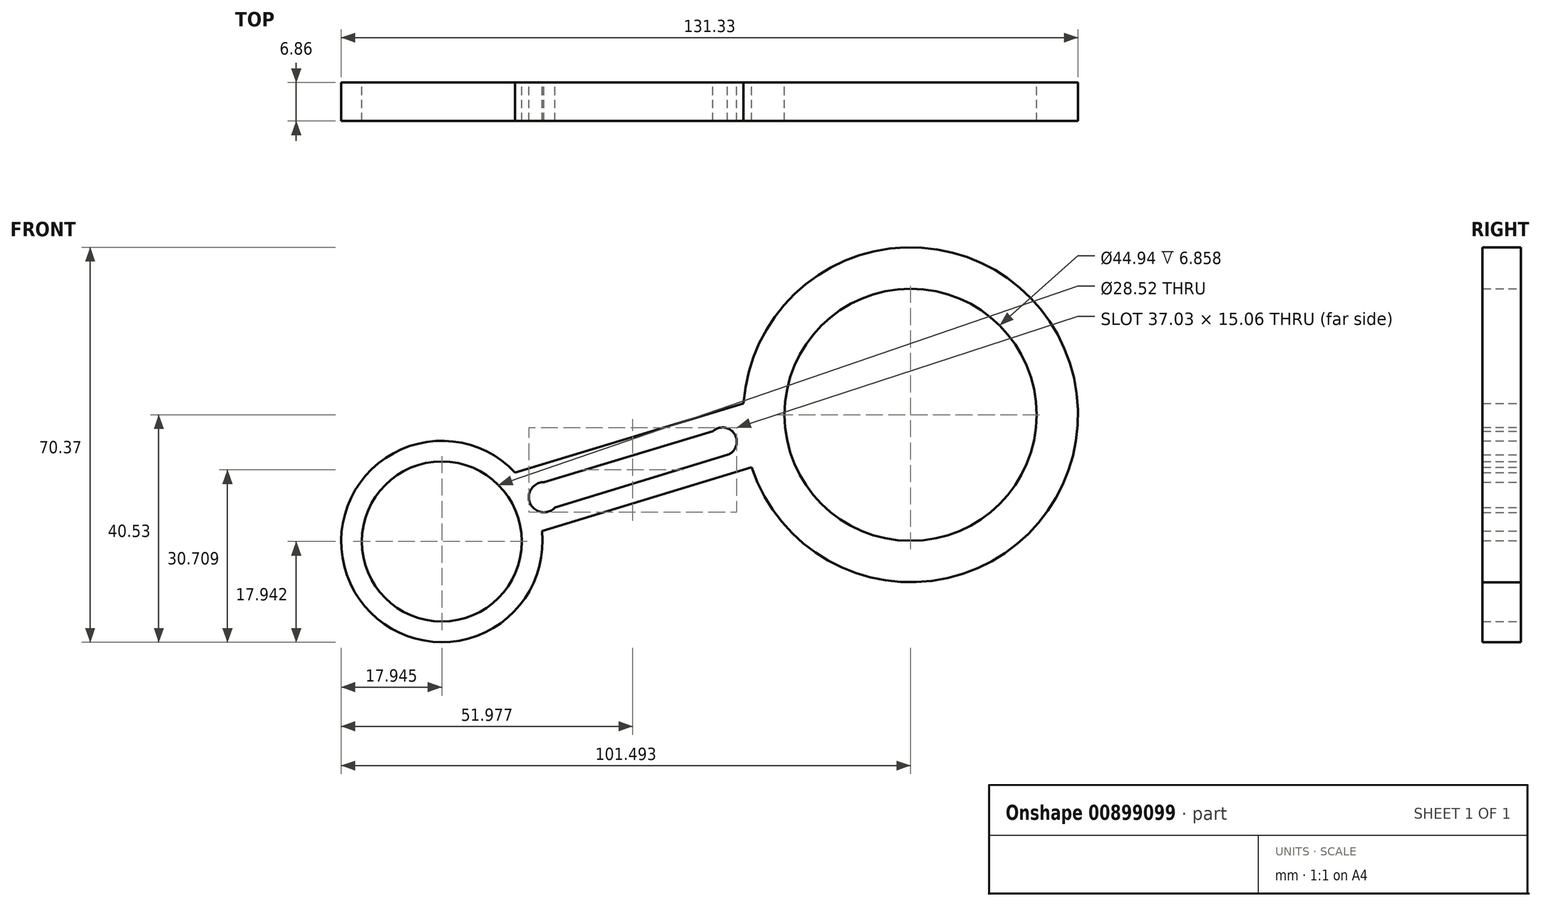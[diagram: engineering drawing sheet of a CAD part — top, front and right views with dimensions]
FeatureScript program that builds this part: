
annotation { "Feature Type Name" : "Feature", "Feature Type Description" : "" }
export const myFeature = defineFeature(function(context is Context, id is Id, definition is map)
    precondition{}
    {
        {
            var Q0;
            Q0=qCreatedBy(makeId("Front.planeOp"),FACE);
            var sketch = newSketch(context, id + "F0", { "sketchPlane" : qUnion([Q0])});
            skArc(sketch, "E0", {"start": v(-52.92, 34.73) * mm, "mid": v(-82.3, 14.98) * mm, "end": v(-48.15, 24.34) * mm});
            skArc(sketch, "E1", {"start": v(-10.77, 35.65) * mm, "mid": v(47.15, 48.8) * mm, "end": v(-12.22, 47.05) * mm});
            skLineSegment(sketch, "E2", {"start": v(-52.92, 34.73) * mm, "end": v(-12.22, 47.05) * mm});
            skLineSegment(sketch, "E3", {"start": v(-48.15, 24.34) * mm, "end": v(-10.77, 35.65) * mm});
            skCircle(sketch, "E4", {"center": v(17.55, 45.04) * mm, "radius": 22.47 * mm});
            skCircle(sketch, "E5", {"center": v(-66, 22.45) * mm, "radius": 14.26 * mm});
            skSolve(sketch);
        }
        {
            var Q0;
            Q0=makeQuery(id+"F0.imprint","IMPRINT",FACE,{"disambiguationData":[TD([[makeQuery(id+"F0.imprint","IMPRINT",EDGE,{"derivedFrom":sQuery(id+"F0.wireOp",EDGE,"E0")}),1.0]])]});
            extrude(context, id + "F1", {"entities" : qUnion([Q0]), "depth" : 6.86 * mm, "offsetDistance" : 25.4 * mm});
        }
        {
            var Q0;
            Q0=qCreatedBy(makeId("Front.planeOp"),FACE);
            var sketch = newSketch(context, id + "F2", { "sketchPlane" : qUnion([Q0])});
            skArc(sketch, "E6", {"start": v(-47.78, 33.03) * mm, "mid": v(-50.27, 29.28) * mm, "end": v(-45.84, 28.5) * mm});
            skArc(sketch, "E7", {"start": v(-15.09, 37.88) * mm, "mid": v(-13.8, 41.57) * mm, "end": v(-17.68, 42.1) * mm});
            skLineSegment(sketch, "E8", {"start": v(-47.78, 33.03) * mm, "end": v(-17.68, 42.1) * mm});
            skLineSegment(sketch, "E9", {"start": v(-45.84, 28.5) * mm, "end": v(-15.09, 37.88) * mm});
            skSolve(sketch);
        }
        {
            var Q0;
            Q0 = qSketchRegion(id + "F2", true);
            var Q1;
            Q1=makeQuery(id+"F1.opExtrude","CAP_FACE",FACE,{"disambiguationData":[OSD([sQuery(id+"F0.wireOp",EDGE,"E0"),sQuery(id+"F0.wireOp",EDGE,"E1"),sQuery(id+"F0.wireOp",EDGE,"E2"),sQuery(id+"F0.wireOp",EDGE,"E3"),sQuery(id+"F0.wireOp",EDGE,"E4"),sQuery(id+"F0.wireOp",EDGE,"E5")])],"isStart":false});
            extrude(context, id + "F3", {"entities" : qUnion([Q0, Q1]), "operationType" : NewBodyOperationType.REMOVE, "depth" : 51.56 * mm, "offsetDistance" : 25.4 * mm});
        }
    });
